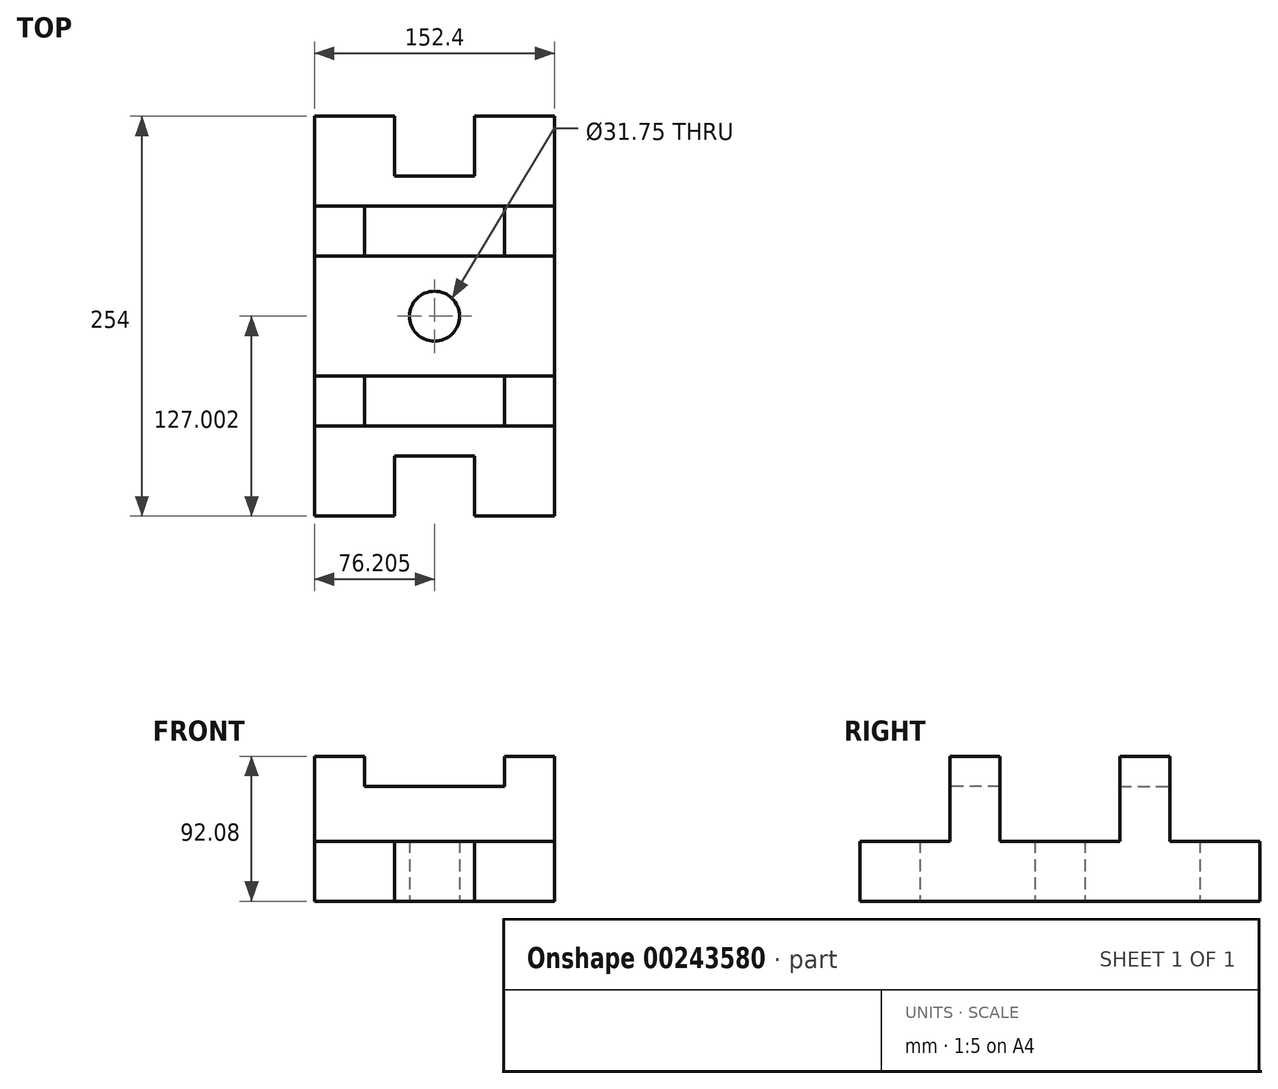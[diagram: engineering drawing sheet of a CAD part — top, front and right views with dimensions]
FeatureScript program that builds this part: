
annotation { "Feature Type Name" : "Feature", "Feature Type Description" : "" }
export const myFeature = defineFeature(function(context is Context, id is Id, definition is map)
    precondition{}
    {
        {
            var Q0;
            Q0=qCreatedBy(makeId("Top.planeOp"),FACE);
            var sketch = newSketch(context, id + "F0", { "sketchPlane" : qUnion([Q0])});
            skLineSegment(sketch, "E0", {"start": v(-1132.25, 301.6) * mm, "end": v(-1132.25, 244.44) * mm});
            skLineSegment(sketch, "E1", {"start": v(-1132.25, 244.44) * mm, "end": v(-1081.45, 244.44) * mm});
            skLineSegment(sketch, "E2", {"start": v(-1081.45, 244.44) * mm, "end": v(-1081.45, 282.54) * mm});
            skLineSegment(sketch, "E3", {"start": v(-1081.45, 282.54) * mm, "end": v(-1030.65, 282.54) * mm});
            skLineSegment(sketch, "E4", {"start": v(-1030.65, 282.54) * mm, "end": v(-1030.65, 244.44) * mm});
            skLineSegment(sketch, "E5", {"start": v(-1030.65, 244.44) * mm, "end": v(-979.85, 244.44) * mm});
            skLineSegment(sketch, "E6", {"start": v(-979.85, 244.44) * mm, "end": v(-979.85, 301.6) * mm});
            skLineSegment(sketch, "E7", {"start": v(-1132.25, 301.6) * mm, "end": v(-979.85, 301.6) * mm});
            skLineSegment(sketch, "E8", {"start": v(-1132.25, 301.6) * mm, "end": v(-1132.25, 333.34) * mm});
            skLineSegment(sketch, "E9", {"start": v(-1132.25, 333.34) * mm, "end": v(-1100.5, 333.34) * mm});
            skLineSegment(sketch, "E10", {"start": v(-1100.5, 333.34) * mm, "end": v(-1100.5, 301.6) * mm});
            skLineSegment(sketch, "E11", {"start": v(-979.85, 301.6) * mm, "end": v(-979.85, 333.34) * mm});
            skLineSegment(sketch, "E12", {"start": v(-979.85, 333.34) * mm, "end": v(-1011.6, 333.34) * mm});
            skLineSegment(sketch, "E13", {"start": v(-1011.6, 333.34) * mm, "end": v(-1011.6, 301.6) * mm});
            skLineSegment(sketch, "E14", {"start": v(-1100.5, 333.34) * mm, "end": v(-1011.6, 333.34) * mm});
            skLineSegment(sketch, "E15", {"start": v(-979.85, 371.44) * mm, "end": v(-979.85, 333.34) * mm});
            skLineSegment(sketch, "E16", {"start": v(-1132.25, 333.34) * mm, "end": v(-1132.25, 371.44) * mm});
            skLineSegment(sketch, "E17.MirrorCS", {"start": v(-1132.25, 409.54) * mm, "end": v(-1132.25, 371.44) * mm});
            skLineSegment(sketch, "E18.MirrorCS", {"start": v(-1132.25, 441.3) * mm, "end": v(-1132.25, 409.54) * mm});
            skLineSegment(sketch, "E19.MirrorCS", {"start": v(-1132.25, 441.3) * mm, "end": v(-1132.25, 498.44) * mm});
            skLineSegment(sketch, "E20.MirrorCS", {"start": v(-1132.25, 498.44) * mm, "end": v(-1081.45, 498.44) * mm});
            skLineSegment(sketch, "E21.MirrorCS", {"start": v(-1081.45, 498.44) * mm, "end": v(-1081.45, 460.34) * mm});
            skLineSegment(sketch, "E22.MirrorCS", {"start": v(-1081.45, 460.34) * mm, "end": v(-1030.65, 460.34) * mm});
            skLineSegment(sketch, "E23.MirrorCS", {"start": v(-1030.65, 460.34) * mm, "end": v(-1030.65, 498.44) * mm});
            skLineSegment(sketch, "E24.MirrorCS", {"start": v(-1030.65, 498.44) * mm, "end": v(-979.85, 498.44) * mm});
            skLineSegment(sketch, "E25.MirrorCS", {"start": v(-979.85, 498.44) * mm, "end": v(-979.85, 441.3) * mm});
            skLineSegment(sketch, "E26.MirrorCS", {"start": v(-979.85, 441.3) * mm, "end": v(-979.85, 409.54) * mm});
            skLineSegment(sketch, "E27.MirrorCS", {"start": v(-979.85, 371.44) * mm, "end": v(-979.85, 409.54) * mm});
            skLineSegment(sketch, "E28.MirrorCS", {"start": v(-1100.5, 409.54) * mm, "end": v(-1011.6, 409.54) * mm});
            skLineSegment(sketch, "E29.MirrorCS", {"start": v(-1132.25, 441.3) * mm, "end": v(-1132.25, 441.3) * mm});
            skLineSegment(sketch, "E30.MirrorCS", {"start": v(-1100.5, 409.54) * mm, "end": v(-1100.5, 441.3) * mm});
            skLineSegment(sketch, "E31.MirrorCS", {"start": v(-1132.25, 409.54) * mm, "end": v(-1100.5, 409.54) * mm});
            skLineSegment(sketch, "E32.MirrorCS", {"start": v(-979.85, 409.54) * mm, "end": v(-1011.6, 409.54) * mm});
            skLineSegment(sketch, "E33.MirrorCS", {"start": v(-1011.6, 409.54) * mm, "end": v(-1011.6, 441.3) * mm});
            skLineSegment(sketch, "E34", {"start": v(-1132.25, 441.3) * mm, "end": v(-979.85, 441.3) * mm});
            skLineSegment(sketch, "E35.MirrorCS", {"start": v(-1056.05, 409.54) * mm, "end": v(-1056.05, 441.3) * mm});
            skCircle(sketch, "E36", {"center": v(-1056.05, 371.44) * mm, "radius": 15.88 * mm});
            skSolve(sketch);
        }
        {
            var Q0;
            {var subQ4=sQuery(id+"F0.wireOp",EDGE,"E0");Q0=makeQuery(id+"F0.imprint","IMPRINT",FACE,{"disambiguationData":[TD([[makeQuery(id+"F0.imprint","IMPRINT",EDGE,{"derivedFrom":subQ4}),1.0]])]});}
            var Q1;
            {var subQ3=sQuery(id+"F0.wireOp",EDGE,"E19.MirrorCS");Q1=makeQuery(id+"F0.imprint","IMPRINT",FACE,{"disambiguationData":[TD([[makeQuery(id+"F0.imprint","IMPRINT",EDGE,{"derivedFrom":subQ3}),-1.0]])]});}
            var Q2;
            {var subQ5=sQuery(id+"F0.wireOp",EDGE,"E21.MirrorCS");Q2=makeQuery(id+"F0.imprint","IMPRINT",FACE,{"disambiguationData":[TD([[makeQuery(id+"F0.imprint","IMPRINT",EDGE,{"derivedFrom":subQ5}),-1.0]])]});}
            extrude(context, id + "F1", {"entities" : qUnion([Q0, Q1, Q2]), "depth" : 38.1 * mm});
        }
        {
            var Q0;
            Q0=makeQuery(id+"F0.imprint","IMPRINT",FACE,{"disambiguationData":[TD([[makeQuery(id+"F0.imprint","IMPRINT",EDGE,{"derivedFrom":sQuery(id+"F0.wireOp",EDGE,"E9")}),1.0]])]});
            extrude(context, id + "F2", {"entities" : qUnion([Q0]), "depth" : 38.1 * mm});
        }
        {
            var Q0;
            {var subQ0=sQuery(id+"F0.wireOp",EDGE,"E18.MirrorCS");Q0=makeQuery(id+"F0.imprint","IMPRINT",FACE,{"disambiguationData":[TD([[makeQuery(id+"F0.imprint","IMPRINT",EDGE,{"derivedFrom":subQ0}),1.0]])]});}
            var Q1;
            {var subQ0=sQuery(id+"F0.wireOp",EDGE,"E26.MirrorCS");Q1=makeQuery(id+"F0.imprint","IMPRINT",FACE,{"disambiguationData":[TD([[makeQuery(id+"F0.imprint","IMPRINT",EDGE,{"derivedFrom":subQ0}),-1.0]])]});}
            var Q2;
            {var subQ0=sQuery(id+"F0.wireOp",EDGE,"E8");Q2=makeQuery(id+"F0.imprint","IMPRINT",FACE,{"disambiguationData":[TD([[makeQuery(id+"F0.imprint","IMPRINT",EDGE,{"derivedFrom":subQ0}),-1.0]])]});}
            var Q3;
            {var subQ0=sQuery(id+"F0.wireOp",EDGE,"E11");Q3=makeQuery(id+"F0.imprint","IMPRINT",FACE,{"disambiguationData":[TD([[makeQuery(id+"F0.imprint","IMPRINT",EDGE,{"derivedFrom":subQ0}),1.0]])]});}
            var Q4;
            Q4=makeQuery(id+"F0.imprint","IMPRINT",FACE,{"disambiguationData":[TD([[makeQuery(id+"F0.imprint","IMPRINT",EDGE,{"derivedFrom":sQuery(id+"F0.wireOp",EDGE,"E31.MirrorCS")}),1.0]])]});
            var Q5;
            Q5=makeQuery(id+"F0.imprint","IMPRINT",FACE,{"disambiguationData":[TD([[makeQuery(id+"F0.imprint","IMPRINT",EDGE,{"derivedFrom":sQuery(id+"F0.wireOp",EDGE,"E32.MirrorCS")}),-1.0]])]});
            extrude(context, id + "F3", {"entities" : qUnion([Q0, Q1, Q2, Q3, Q4, Q5]), "operationType" : NewBodyOperationType.ADD, "depth" : 92.07 * mm});
        }
        {
            var Q0;
            Q0=makeQuery(id+"F0.imprint","IMPRINT",FACE,{"disambiguationData":[TD([[makeQuery(id+"F0.imprint","IMPRINT",EDGE,{"derivedFrom":sQuery(id+"F0.wireOp",EDGE,"E28.MirrorCS")}),1.0]])]});
            var Q1;
            Q1=makeQuery(id+"F0.imprint","IMPRINT",FACE,{"disambiguationData":[TD([[makeQuery(id+"F0.imprint","IMPRINT",EDGE,{"derivedFrom":sQuery(id+"F0.wireOp",EDGE,"E28.MirrorCS")}),1.0]])]});
            var Q2;
            {var subQ0=sQuery(id+"F0.wireOp",EDGE,"E10");Q2=makeQuery(id+"F0.imprint","IMPRINT",FACE,{"disambiguationData":[TD([[makeQuery(id+"F0.imprint","IMPRINT",EDGE,{"derivedFrom":subQ0}),1.0]])]});}
            extrude(context, id + "F4", {"entities" : qUnion([Q0, Q1, Q2]), "operationType" : NewBodyOperationType.ADD, "depth" : 73.02 * mm});
        }
        {
            var Q0;
            Q0=makeQuery(id+"F0.imprint","IMPRINT",FACE,{"disambiguationData":[TD([[makeQuery(id+"F0.imprint","IMPRINT",EDGE,{"derivedFrom":sQuery(id+"F0.wireOp",EDGE,"E36")}),1.0]])]});
            extrude(context, id + "F5", {"entities" : qUnion([Q0]), "operationType" : NewBodyOperationType.REMOVE, "oppositeDirection" : true, "depth" : 76.2 * mm});
        }
    });
